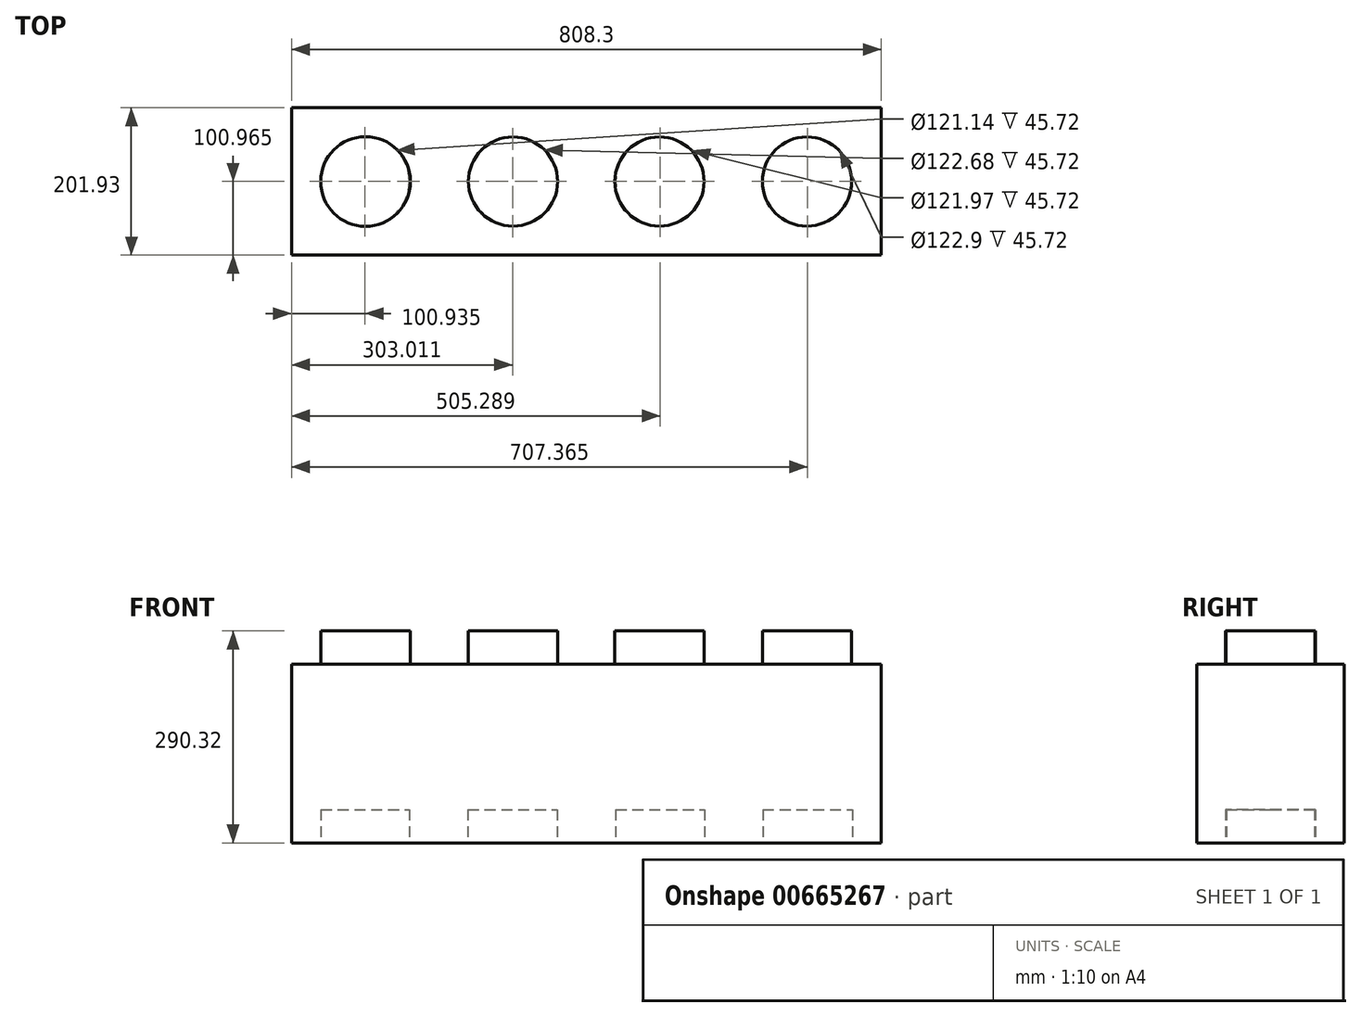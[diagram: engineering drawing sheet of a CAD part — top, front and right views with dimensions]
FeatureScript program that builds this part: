
annotation { "Feature Type Name" : "Feature", "Feature Type Description" : "" }
export const myFeature = defineFeature(function(context is Context, id is Id, definition is map)
    precondition{}
    {
        {
            var Q0;
            Q0=qCreatedBy(makeId("Front.planeOp"),FACE);
            var sketch = newSketch(context, id + "F0", { "sketchPlane" : qUnion([Q0])});
            skLineSegment(sketch, "E0.bottom", {"start": v(404.15, 122.3) * mm, "end": v(-404.15, 122.3) * mm});
            skLineSegment(sketch, "E0.top", {"start": v(404.15, -122.3) * mm, "end": v(-404.15, -122.3) * mm});
            skLineSegment(sketch, "E0.left", {"start": v(404.15, 122.3) * mm, "end": v(404.15, -122.3) * mm});
            skLineSegment(sketch, "E0.right", {"start": v(-404.15, 122.3) * mm, "end": v(-404.15, -122.3) * mm});
            skPoint(sketch, "E0.middle", {"position": v(0, 0) * mm});
            skSolve(sketch);
        }
        {
            var Q0;
            Q0=makeQuery(id+"F0.imprint","IMPRINT",FACE,{"disambiguationData":[TD([[makeQuery(id+"F0.imprint","IMPRINT",EDGE,{"derivedFrom":sQuery(id+"F0.wireOp",EDGE,"E0.bottom")}),1.0]])]});
            extrude(context, id + "F1", {"entities" : qUnion([Q0]), "depth" : 201.93 * mm, "offsetDistance" : 25.4 * mm});
        }
        {
            var Q0;
            Q0=makeQuery(id+"F1.opExtrude","SWEPT_FACE",FACE,{"disambiguationData":[OSD([sQuery(id+"F0.wireOp",EDGE,"E0.bottom")])]});
            var sketch = newSketch(context, id + "F2", { "sketchPlane" : qUnion([Q0])});
            skLineSegment(sketch, "E1.bottom", {"start": v(-404.15, -201.93) * mm, "end": v(-201.1, -201.93) * mm});
            skLineSegment(sketch, "E1.top", {"start": v(-404.15, 0) * mm, "end": v(-201.1, 0) * mm});
            skLineSegment(sketch, "E1.left", {"start": v(-404.15, -201.93) * mm, "end": v(-404.15, 0) * mm});
            skCircle(sketch, "E2", {"center": v(-302.63, -100.97) * mm, "radius": 61.43 * mm});
            skLineSegment(sketch, "E3.bottom", {"start": v(-201.1, -201.93) * mm, "end": v(0, -201.93) * mm});
            skLineSegment(sketch, "E3.top", {"start": v(-201.1, 0) * mm, "end": v(0, 0) * mm});
            skLineSegment(sketch, "E4.bottom", {"start": v(0, -201.93) * mm, "end": v(200.23, -201.93) * mm});
            skLineSegment(sketch, "E4.top", {"start": v(0, 0) * mm, "end": v(200.23, 0) * mm});
            skLineSegment(sketch, "E5.bottom", {"start": v(200.23, -201.93) * mm, "end": v(404.15, -201.93) * mm});
            skLineSegment(sketch, "E5.top", {"start": v(200.23, 0) * mm, "end": v(404.15, 0) * mm});
            skCircle(sketch, "E6", {"center": v(-100.55, -100.97) * mm, "radius": 61.09 * mm});
            skCircle(sketch, "E7", {"center": v(100.12, -100.97) * mm, "radius": 61.09 * mm});
            skCircle(sketch, "E8", {"center": v(302.2, -100.97) * mm, "radius": 61.17 * mm});
            skSolve(sketch);
        }
        {
            var Q0;
            Q0=makeQuery(id+"F2.imprint","IMPRINT",FACE,{"disambiguationData":[TD([[makeQuery(id+"F2.imprint","IMPRINT",EDGE,{"derivedFrom":sQuery(id+"F2.wireOp",EDGE,"E6")}),1.0]])]});
            var Q1;
            Q1=makeQuery(id+"F2.imprint","IMPRINT",FACE,{"disambiguationData":[TD([[makeQuery(id+"F2.imprint","IMPRINT",EDGE,{"derivedFrom":sQuery(id+"F2.wireOp",EDGE,"E7")}),1.0]])]});
            var Q2;
            Q2=makeQuery(id+"F2.imprint","IMPRINT",FACE,{"disambiguationData":[TD([[makeQuery(id+"F2.imprint","IMPRINT",EDGE,{"derivedFrom":sQuery(id+"F2.wireOp",EDGE,"E8")}),1.0]])]});
            var Q3;
            Q3=makeQuery(id+"F2.imprint","IMPRINT",FACE,{"disambiguationData":[TD([[makeQuery(id+"F2.imprint","IMPRINT",EDGE,{"derivedFrom":sQuery(id+"F2.wireOp",EDGE,"E2")}),1.0]])]});
            extrude(context, id + "F3", {"entities" : qUnion([Q0, Q1, Q2, Q3]), "operationType" : NewBodyOperationType.ADD, "depth" : 45.72 * mm, "offsetDistance" : 25.4 * mm});
        }
        {
            var Q0;
            Q0=makeQuery(id+"F1.opExtrude","SWEPT_FACE",FACE,{"disambiguationData":[OSD([sQuery(id+"F0.wireOp",EDGE,"E0.top")])]});
            var sketch = newSketch(context, id + "F4", { "sketchPlane" : qUnion([Q0])});
            skLineSegment(sketch, "E9.bottom", {"start": v(-404.15, 0) * mm, "end": v(-202.28, 0) * mm});
            skLineSegment(sketch, "E9.top", {"start": v(-404.15, 201.93) * mm, "end": v(-202.28, 201.93) * mm});
            skLineSegment(sketch, "E9.left", {"start": v(-404.15, 0) * mm, "end": v(-404.15, 201.93) * mm});
            skLineSegment(sketch, "E9.right", {"start": v(-202.28, 0) * mm, "end": v(-202.28, 201.93) * mm});
            skLineSegment(sketch, "E10.bottom", {"start": v(-202.28, 0) * mm, "end": v(0, 0) * mm});
            skLineSegment(sketch, "E10.top", {"start": v(-202.28, 201.93) * mm, "end": v(0, 201.93) * mm});
            skLineSegment(sketch, "E10.right", {"start": v(0, 0) * mm, "end": v(0, 201.93) * mm});
            skLineSegment(sketch, "E11.bottom", {"start": v(0, 0) * mm, "end": v(202.28, 0) * mm});
            skLineSegment(sketch, "E11.top", {"start": v(0, 201.93) * mm, "end": v(202.28, 201.93) * mm});
            skLineSegment(sketch, "E11.right", {"start": v(202.28, 0) * mm, "end": v(202.28, 201.93) * mm});
            skLineSegment(sketch, "E12.bottom", {"start": v(202.28, 0) * mm, "end": v(404.15, 0) * mm});
            skLineSegment(sketch, "E12.top", {"start": v(202.28, 201.93) * mm, "end": v(404.15, 201.93) * mm});
            skLineSegment(sketch, "E12.right", {"start": v(404.15, 0) * mm, "end": v(404.15, 201.93) * mm});
            skCircle(sketch, "E13", {"center": v(-303.21, 100.97) * mm, "radius": 60.57 * mm});
            skCircle(sketch, "E14", {"center": v(-101.14, 100.97) * mm, "radius": 61.34 * mm});
            skCircle(sketch, "E15", {"center": v(101.14, 100.97) * mm, "radius": 60.99 * mm});
            skCircle(sketch, "E16", {"center": v(303.21, 100.97) * mm, "radius": 61.45 * mm});
            skSolve(sketch);
        }
        {
            var Q0;
            Q0=makeQuery(id+"F4.imprint","IMPRINT",FACE,{"disambiguationData":[TD([[makeQuery(id+"F4.imprint","IMPRINT",EDGE,{"derivedFrom":sQuery(id+"F4.wireOp",EDGE,"E16")}),1.0]])]});
            var Q1;
            Q1=makeQuery(id+"F4.imprint","IMPRINT",FACE,{"disambiguationData":[TD([[makeQuery(id+"F4.imprint","IMPRINT",EDGE,{"derivedFrom":sQuery(id+"F4.wireOp",EDGE,"E15")}),1.0]])]});
            var Q2;
            Q2=makeQuery(id+"F4.imprint","IMPRINT",FACE,{"disambiguationData":[TD([[makeQuery(id+"F4.imprint","IMPRINT",EDGE,{"derivedFrom":sQuery(id+"F4.wireOp",EDGE,"E14")}),1.0]])]});
            var Q3;
            Q3=makeQuery(id+"F4.imprint","IMPRINT",FACE,{"disambiguationData":[TD([[makeQuery(id+"F4.imprint","IMPRINT",EDGE,{"derivedFrom":sQuery(id+"F4.wireOp",EDGE,"E13")}),1.0]])]});
            extrude(context, id + "F5", {"entities" : qUnion([Q0, Q1, Q2, Q3]), "operationType" : NewBodyOperationType.REMOVE, "oppositeDirection" : true, "depth" : 45.72 * mm, "offsetDistance" : 25.4 * mm});
        }
    });
